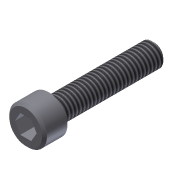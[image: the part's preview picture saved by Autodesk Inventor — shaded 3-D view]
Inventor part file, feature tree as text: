
AUTODESK INVENTOR PART (.ipt)
format: ipt  version: 2011 (Build 150239000, 239)  size: 104,448 bytes
history: native  units: in
note: dims shown in document units (in); Inventor stores cm internally (conversion verified against a paired STEP export)
features: extrude x3, sketch x3, chamfer x2, thread x1
ambient origin geometry x8: Origin, YZ Plane, XZ Plane, XY Plane, X Axis, Y Axis, Z Axis, Center Point
bodies: Solid1 (feature_tree)
feature tree (9):
  extrude  "Extrusion1"  Depth=0.19in TaperAngle=0.0deg
  extrude  "Extrusion2"  Depth=0.875in TaperAngle=0.0deg
  extrude  "Extrusion3"  Depth=0.125in TaperAngle=0.0deg
  thread  "Thread1"  [1 undecoded]
  chamfer  "Chamfer1"  [1 undecoded]
  chamfer  "Chamfer2"  [1 undecoded]
  sketch  "Sketch1"  dims[d0=0.312in d1=0.19in d2=0.0in]
  sketch  "Sketch2"  dims[d3=0.19in d4=0.875in d5=0.0in]
  sketch  "Sketch3"  dims[d6=0.1562in d7=0.125in d8=0.0in d9=1.0in d10=0.0in d11=0.02in d12=0.125in d13=45.0deg d14=0.02in d15=0.125in d16=45.0deg]
note: 3 required parameter values undecoded (feature->parameter linkage not recoverable at this tier; creation-order binding heuristic only, values carry confidence <= 0.55)
